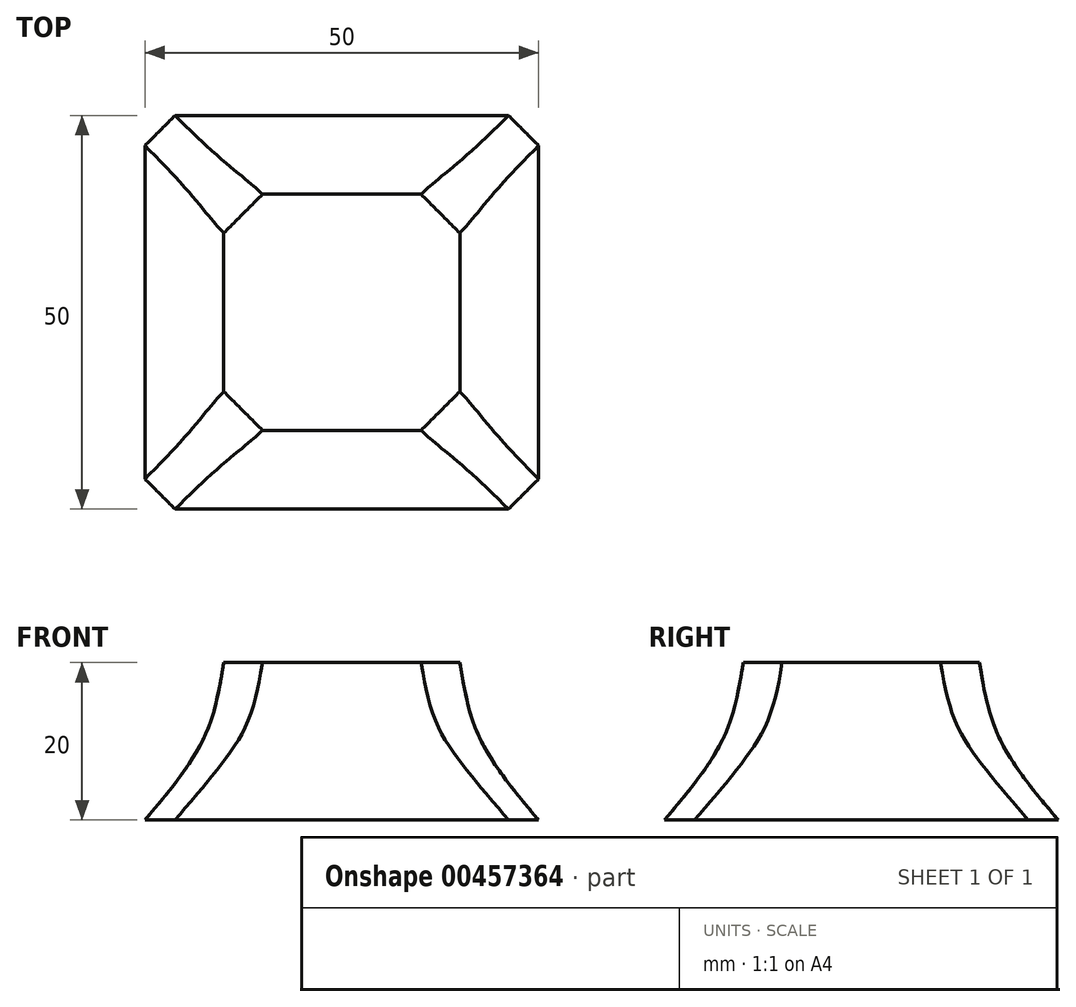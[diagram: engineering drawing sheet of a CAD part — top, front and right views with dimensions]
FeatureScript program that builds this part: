
annotation { "Feature Type Name" : "Feature", "Feature Type Description" : "" }
export const myFeature = defineFeature(function(context is Context, id is Id, definition is map)
    precondition{}
    {
        {
            var Q0;
            Q0=qCreatedBy(makeId("Top.planeOp"),FACE);
            var sketch = newSketch(context, id + "F0", { "sketchPlane" : qUnion([Q0])});
            skLineSegment(sketch, "E0.bottom", {"start": v(25, 25) * mm, "end": v(-25, 25) * mm});
            skLineSegment(sketch, "E0.top", {"start": v(25, -25) * mm, "end": v(-25, -25) * mm});
            skLineSegment(sketch, "E0.left", {"start": v(25, 25) * mm, "end": v(25, -25) * mm});
            skLineSegment(sketch, "E0.right", {"start": v(-25, 25) * mm, "end": v(-25, -25) * mm});
            skPoint(sketch, "E0.middle", {"position": v(0, 0) * mm});
            skSolve(sketch);
        }
        {
            var Q0;
            Q0 = qSketchRegion(id + "F0", true);
            extrude(context, id + "F1", {"entities" : qUnion([Q0]), "depth" : 20 * mm});
        }
        {
            var Q0;
            Q0=makeQuery(id+"F1.opExtrude","SWEPT_FACE",FACE,{"disambiguationData":[OSD([sQuery(id+"F0.wireOp",EDGE,"E0.top")])]});
            var sketch = newSketch(context, id + "F2", { "sketchPlane" : qUnion([Q0])});
            skFitSpline(sketch, "E1", {"points": [v(-25, 0) * mm, v(-17.51, 10.44) * mm, v(-15, 20) * mm], "startDerivative": vector(16.37, 19.37) * mm, "endDerivative": vector(3.35, 20.65) * mm});
            skFitSpline(sketch, "E2", {"points": [v(-25, 0) * mm, v(-25, 20) * mm], "startDerivative": vector(0, 20) * mm, "endDerivative": vector(0, 20) * mm});
            skFitSpline(sketch, "E3", {"points": [v(-25, 20) * mm, v(-15, 20) * mm], "startDerivative": vector(10, 0) * mm, "endDerivative": vector(10, 0) * mm});
            skFitSpline(sketch, "E4.MirrorCS", {"points": [v(25, 0) * mm, v(17.51, 10.44) * mm, v(15, 20) * mm], "startDerivative": vector(-16.37, 19.37) * mm, "endDerivative": vector(-3.35, 20.65) * mm});
            skFitSpline(sketch, "E5.MirrorCS", {"points": [v(25, 0) * mm, v(25, 20) * mm], "startDerivative": vector(0, 20) * mm, "endDerivative": vector(0, 20) * mm});
            skLineSegment(sketch, "E6", {"start": v(15, 20) * mm, "end": v(25, 20) * mm});
            skSolve(sketch);
        }
        {
            var Q0;
            Q0=makeQuery(id+"F1.opExtrude","SWEPT_FACE",FACE,{"disambiguationData":[OSD([sQuery(id+"F0.wireOp",EDGE,"E0.left")])]});
            var sketch = newSketch(context, id + "F3", { "sketchPlane" : qUnion([Q0])});
            skFitSpline(sketch, "E7", {"points": [v(-25, 0) * mm, v(-17.51, 10.44) * mm, v(-15, 20) * mm], "startDerivative": vector(16.37, 19.37) * mm, "endDerivative": vector(3.35, 20.65) * mm});
            skFitSpline(sketch, "E8", {"points": [v(-25, 0) * mm, v(-25, 20) * mm], "startDerivative": vector(0, 20) * mm, "endDerivative": vector(0, 20) * mm});
            skFitSpline(sketch, "E9", {"points": [v(-25, 20) * mm, v(-15, 20) * mm], "startDerivative": vector(10, 0) * mm, "endDerivative": vector(10, 0) * mm});
            skFitSpline(sketch, "E10.MirrorCS", {"points": [v(25, 0) * mm, v(17.51, 10.44) * mm, v(15, 20) * mm], "startDerivative": vector(-16.37, 19.37) * mm, "endDerivative": vector(-3.35, 20.65) * mm});
            skFitSpline(sketch, "E11.MirrorCS", {"points": [v(25, 0) * mm, v(25, 20) * mm], "startDerivative": vector(0, 20) * mm, "endDerivative": vector(0, 20) * mm});
            skLineSegment(sketch, "E12", {"start": v(15, 20) * mm, "end": v(25, 20) * mm});
            skSolve(sketch);
        }
        {
            var Q0;
            Q0 = qSketchRegion(id + "F2", true);
            extrude(context, id + "F4", {"entities" : qUnion([Q0]), "operationType" : NewBodyOperationType.REMOVE, "oppositeDirection" : true, "depth" : 50 * mm});
        }
        {
            var Q0;
            Q0 = qSketchRegion(id + "F3", true);
            extrude(context, id + "F5", {"entities" : qUnion([Q0]), "operationType" : NewBodyOperationType.REMOVE, "oppositeDirection" : true, "depth" : 50 * mm});
        }
        {
            var Q0;
            Q0=makeQuery(id+"F5.boolean.opBoolean","INTERSECT",EDGE,{"derivedFrom":[makeQuery(id+"F4.boolean.opBoolean","COPY",FACE,{"derivedFrom":makeQuery(id+"F4.opExtrude","SWEPT_FACE",FACE,{"disambiguationData":[OSD([sQuery(id+"F2.wireOp",EDGE,"E4.MirrorCS")])]})}),makeQuery(id+"F5.opExtrude","SWEPT_FACE",FACE,{"disambiguationData":[OSD([sQuery(id+"F3.wireOp",EDGE,"E10.MirrorCS")])]})]});
            var Q1;
            Q1=makeQuery(id+"F5.boolean.opBoolean","INTERSECT",EDGE,{"derivedFrom":[makeQuery(id+"F4.boolean.opBoolean","COPY",FACE,{"derivedFrom":makeQuery(id+"F4.opExtrude","SWEPT_FACE",FACE,{"disambiguationData":[OSD([sQuery(id+"F2.wireOp",EDGE,"E4.MirrorCS")])]})}),makeQuery(id+"F5.opExtrude","SWEPT_FACE",FACE,{"disambiguationData":[OSD([sQuery(id+"F3.wireOp",EDGE,"E7")])]})]});
            var Q2;
            Q2=makeQuery(id+"F5.boolean.opBoolean","INTERSECT",EDGE,{"derivedFrom":[makeQuery(id+"F4.boolean.opBoolean","COPY",FACE,{"derivedFrom":makeQuery(id+"F4.opExtrude","SWEPT_FACE",FACE,{"disambiguationData":[OSD([sQuery(id+"F2.wireOp",EDGE,"E1")])]})}),makeQuery(id+"F5.opExtrude","SWEPT_FACE",FACE,{"disambiguationData":[OSD([sQuery(id+"F3.wireOp",EDGE,"E7")])]})]});
            var Q3;
            Q3=makeQuery(id+"F5.boolean.opBoolean","INTERSECT",EDGE,{"derivedFrom":[makeQuery(id+"F4.boolean.opBoolean","COPY",FACE,{"derivedFrom":makeQuery(id+"F4.opExtrude","SWEPT_FACE",FACE,{"disambiguationData":[OSD([sQuery(id+"F2.wireOp",EDGE,"E1")])]})}),makeQuery(id+"F5.opExtrude","SWEPT_FACE",FACE,{"disambiguationData":[OSD([sQuery(id+"F3.wireOp",EDGE,"E10.MirrorCS")])]})]});
            chamfer(context, id + "F6", {"entities" : qUnion([Q0, Q1, Q2, Q3]), "width" : 5 * mm, "tangentPropagation" : true});
        }
    });
